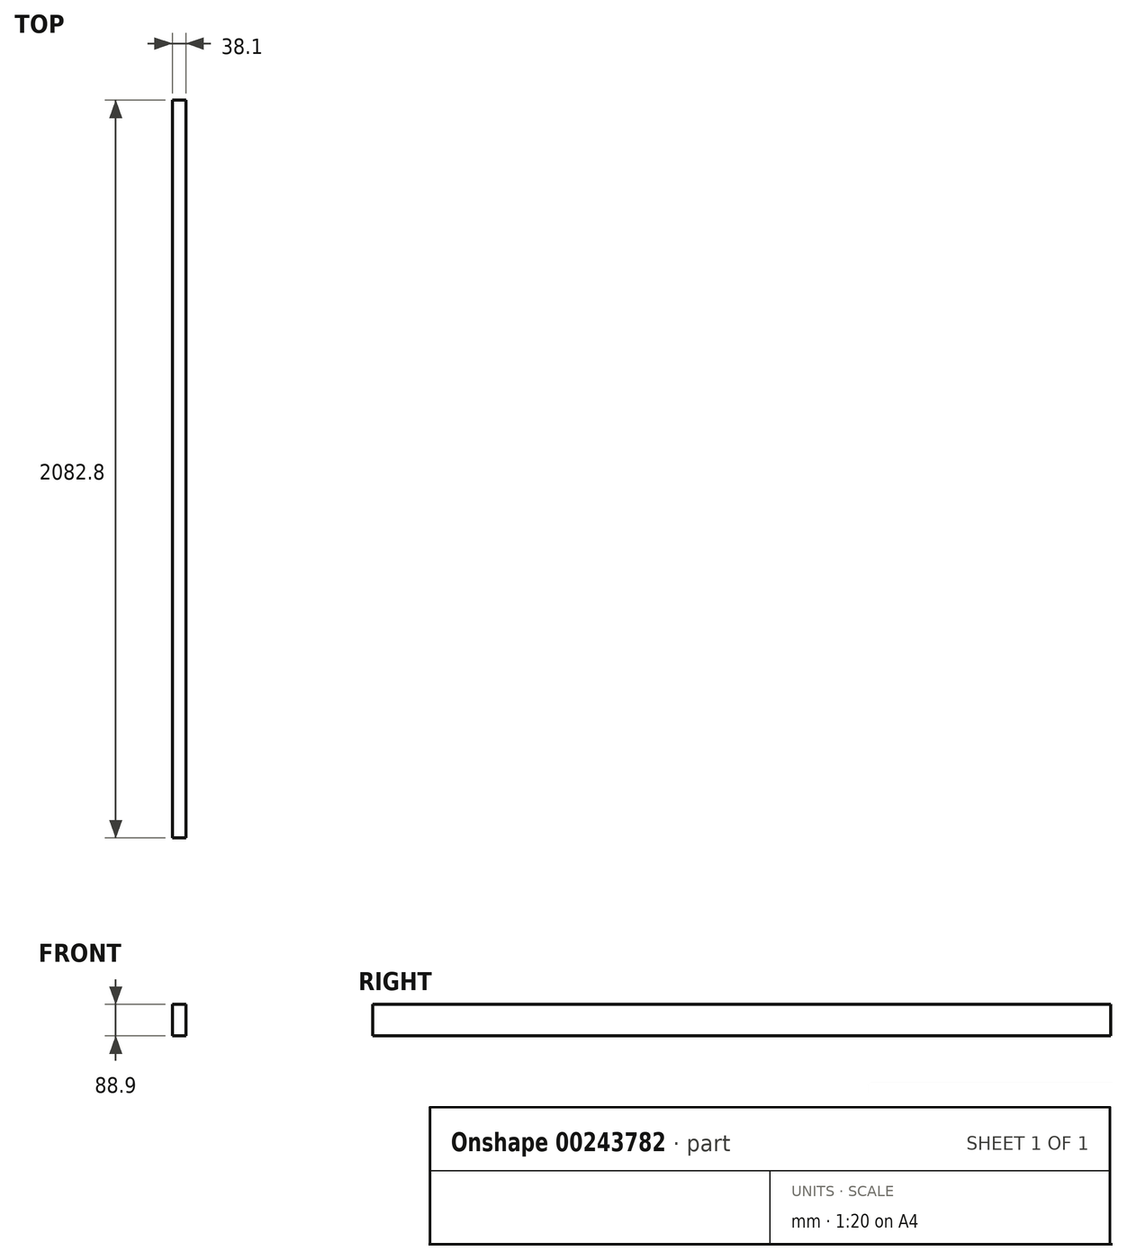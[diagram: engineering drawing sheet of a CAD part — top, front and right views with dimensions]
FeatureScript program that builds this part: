
annotation { "Feature Type Name" : "Feature", "Feature Type Description" : "" }
export const myFeature = defineFeature(function(context is Context, id is Id, definition is map)
    precondition{}
    {
        {
            var Q0;
            Q0=qCreatedBy(makeId("Front.planeOp"),FACE);
            var sketch = newSketch(context, id + "F0", { "sketchPlane" : qUnion([Q0])});
            skLineSegment(sketch, "E0.bottom", {"start": v(-38.1, 88.9) * mm, "end": v(0, 88.9) * mm});
            skLineSegment(sketch, "E0.top", {"start": v(-38.1, 0) * mm, "end": v(0, 0) * mm});
            skLineSegment(sketch, "E0.left", {"start": v(-38.1, 88.9) * mm, "end": v(-38.1, 0) * mm});
            skLineSegment(sketch, "E0.right", {"start": v(0, 88.9) * mm, "end": v(0, 0) * mm});
            skSolve(sketch);
        }
        {
            var Q0;
            Q0=makeQuery(id+"F0.imprint","IMPRINT",FACE,{"disambiguationData":[TD([[makeQuery(id+"F0.imprint","IMPRINT",EDGE,{"derivedFrom":sQuery(id+"F0.wireOp",EDGE,"E0.bottom")}),-1.0]])]});
            extrude(context, id + "F1", {"entities" : qUnion([Q0]), "depth" : 2082.8 * mm});
        }
    });
